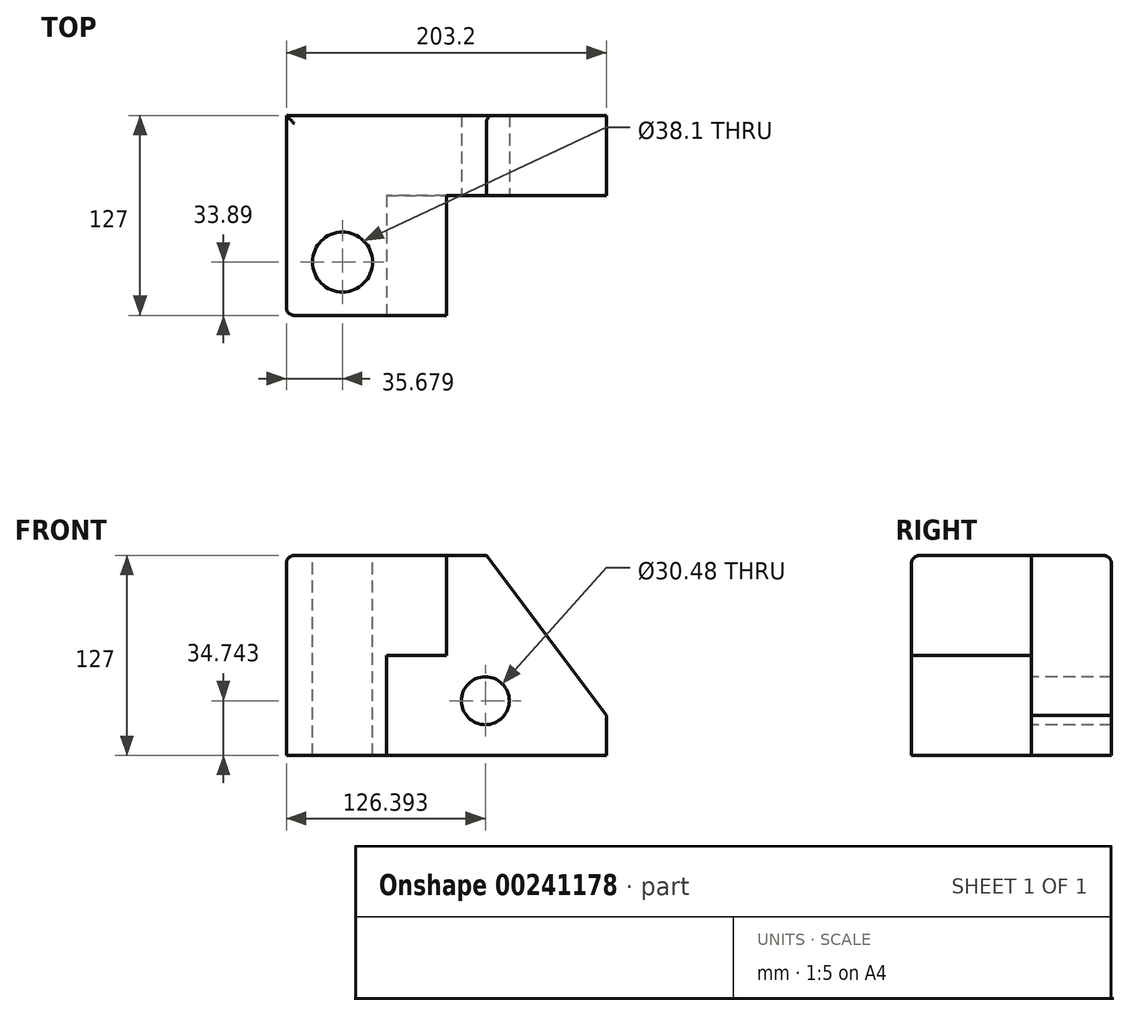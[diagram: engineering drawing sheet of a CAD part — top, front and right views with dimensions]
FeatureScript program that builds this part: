
annotation { "Feature Type Name" : "Feature", "Feature Type Description" : "" }
export const myFeature = defineFeature(function(context is Context, id is Id, definition is map)
    precondition{}
    {
        {
            var Q0;
            Q0=qCreatedBy(makeId("Front.planeOp"),FACE);
            var sketch = newSketch(context, id + "F0", { "sketchPlane" : qUnion([Q0])});
            skPoint(sketch, "E0.start.orphan", {"position": v(0, -60.78) * mm});
            skLineSegment(sketch, "E1", {"start": v(-88.74, -63.95) * mm, "end": v(114.46, -63.95) * mm});
            skLineSegment(sketch, "E2", {"start": v(114.46, -63.95) * mm, "end": v(114.46, 63.05) * mm});
            skLineSegment(sketch, "E3", {"start": v(-88.74, -63.95) * mm, "end": v(-88.74, 63.05) * mm});
            skLineSegment(sketch, "E4", {"start": v(-88.74, 63.05) * mm, "end": v(114.46, 63.05) * mm});
            skSolve(sketch);
        }
        {
            var Q0;
            Q0 = qSketchRegion(id + "F0", true);
            extrude(context, id + "F1", {"entities" : qUnion([Q0]), "depth" : 127 * mm});
        }
        {
            var Q0;
            Q0=makeQuery(id+"F1.opExtrude","CAP_FACE",FACE,{"disambiguationData":[OSD([sQuery(id+"F0.wireOp",EDGE,"E1"),sQuery(id+"F0.wireOp",EDGE,"E2"),sQuery(id+"F0.wireOp",EDGE,"E3"),sQuery(id+"F0.wireOp",EDGE,"E4")])],"isStart":false});
            var sketch = newSketch(context, id + "F2", { "sketchPlane" : qUnion([Q0])});
            skLineSegment(sketch, "E5", {"start": v(-88.74, 63.05) * mm, "end": v(12.86, 63.05) * mm});
            skLineSegment(sketch, "E6", {"start": v(12.86, 63.05) * mm, "end": v(12.86, -0.45) * mm});
            skLineSegment(sketch, "E7", {"start": v(12.86, -0.45) * mm, "end": v(-25.24, -0.45) * mm});
            skLineSegment(sketch, "E8", {"start": v(-25.24, -0.45) * mm, "end": v(-25.24, -63.95) * mm});
            skLineSegment(sketch, "E9", {"start": v(-25.24, -63.95) * mm, "end": v(-88.74, -63.95) * mm});
            skLineSegment(sketch, "E10", {"start": v(-88.74, -63.95) * mm, "end": v(-88.74, 63.05) * mm});
            skSolve(sketch);
        }
        {
            var Q0;
            {var subQ3=sQuery(id+"F2.wireOp",EDGE,"E6");Q0=makeQuery(id+"F2.imprint","IMPRINT",FACE,{"disambiguationData":[TD([[makeQuery(id+"F2.imprint","IMPRINT",EDGE,{"derivedFrom":subQ3}),1.0]])]});}
            extrude(context, id + "F3", {"entities" : qUnion([Q0]), "operationType" : NewBodyOperationType.REMOVE, "oppositeDirection" : true, "depth" : 76.2 * mm});
        }
        {
            var Q0;
            Q0=makeQuery(id+"F1.opExtrude","SWEPT_EDGE",EDGE,{"disambiguationData":[OSD([sQuery(id+"F0.wireOp",EDGE,"E2"),sQuery(id+"F0.wireOp",EDGE,"E4")])]});
            chamfer(context, id + "F4", {"entities" : qUnion([Q0]), "chamferType" : ChamferType.TWO_OFFSETS, "width1" : 76.2 * mm, "oppositeDirection" : false, "width2" : 101.6 * mm, "tangentPropagation" : true});
        }
        {
            var Q0;
            Q0=makeQuery(id+"F1.opExtrude","CAP_EDGE",EDGE,{"disambiguationData":[OSD([sQuery(id+"F0.wireOp",EDGE,"E4")])],"isStart":false});
            var Q1;
            Q1=makeQuery(id+"F1.opExtrude","SWEPT_EDGE",EDGE,{"disambiguationData":[OSD([sQuery(id+"F0.wireOp",EDGE,"E3"),sQuery(id+"F0.wireOp",EDGE,"E4")])]});
            var Q2;
            Q2=makeQuery(id+"F3.boolean.opBoolean","COPY",EDGE,{"derivedFrom":makeQuery(id+"F3.opExtrude","SWEPT_EDGE",EDGE,{"disambiguationData":[OSD([sQuery(id+"F0.wireOp",EDGE,"E4"),sQuery(id+"F2.wireOp",EDGE,"E5"),sQuery(id+"F2.wireOp",EDGE,"E6")])]})});
            var Q3;
            Q3=makeQuery(id+"F3.boolean.opBoolean","COPY",EDGE,{"derivedFrom":makeQuery(id+"F3.opExtrude","CAP_EDGE",EDGE,{"disambiguationData":[OSD([sQuery(id+"F0.wireOp",EDGE,"E4")])],"isStart":false})});
            var Q4;
            Q4=makeQuery(id+"F1.opExtrude","CAP_EDGE",EDGE,{"disambiguationData":[OSD([sQuery(id+"F0.wireOp",EDGE,"E4")])],"isStart":true});
            fillet(context, id + "F5", {"entities" : qUnion([Q0, Q1, Q2, Q3, Q4]), "radius" : 5.08 * mm, "tangentPropagation" : true, "allowEdgeOverflow" : false});
        }
        {
            var Q0;
            Q0=makeQuery(id+"F3.boolean.opBoolean","COPY",EDGE,{"derivedFrom":makeQuery(id+"F3.opExtrude","CAP_EDGE",EDGE,{"disambiguationData":[OSD([sQuery(id+"F2.wireOp",EDGE,"E8")])],"isStart":true})});
            var Q1;
            Q1=makeQuery(id+"F1.opExtrude","CAP_EDGE",EDGE,{"disambiguationData":[OSD([sQuery(id+"F0.wireOp",EDGE,"E3")])],"isStart":false});
            fillet(context, id + "F6", {"entities" : qUnion([Q0, Q1]), "radius" : 5.08 * mm, "tangentPropagation" : true, "allowEdgeOverflow" : false});
        }
        {
            var Q0;
            Q0=makeQuery(id+"F3.boolean.opBoolean","COPY",FACE,{"derivedFrom":makeQuery(id+"F3.opExtrude","CAP_FACE",FACE,{"disambiguationData":[OSD([sQuery(id+"F0.wireOp",EDGE,"E1"),sQuery(id+"F0.wireOp",EDGE,"E2"),sQuery(id+"F0.wireOp",EDGE,"E4"),sQuery(id+"F2.wireOp",EDGE,"E6"),sQuery(id+"F2.wireOp",EDGE,"E7"),sQuery(id+"F2.wireOp",EDGE,"E8")])],"isStart":false})});
            var sketch = newSketch(context, id + "F7", { "sketchPlane" : qUnion([Q0])});
            skCircle(sketch, "E11", {"center": v(37.65, -29.2) * mm, "radius": 15.24 * mm});
            skSolve(sketch);
        }
        {
            var Q0;
            Q0=makeQuery(id+"F7.imprint","IMPRINT",FACE,{"disambiguationData":[TD([[makeQuery(id+"F7.imprint","IMPRINT",EDGE,{"derivedFrom":sQuery(id+"F7.wireOp",EDGE,"E11")}),1.0]])]});
            var Q1;
            Q1=makeQuery(id+"F1.opExtrude","CAP_FACE",FACE,{"disambiguationData":[OSD([sQuery(id+"F0.wireOp",EDGE,"E1"),sQuery(id+"F0.wireOp",EDGE,"E2"),sQuery(id+"F0.wireOp",EDGE,"E3"),sQuery(id+"F0.wireOp",EDGE,"E4")])],"isStart":true});
            extrude(context, id + "F8", {"entities" : qUnion([Q0]), "operationType" : NewBodyOperationType.REMOVE, "endBound" : BoundingType.UP_TO_SURFACE, "oppositeDirection" : true, "endBoundEntityFace" : qUnion([Q1]), "depth" : 25.4 * mm});
        }
        {
            var Q0;
            Q0=makeQuery(id+"F1.opExtrude","SWEPT_FACE",FACE,{"disambiguationData":[OSD([sQuery(id+"F0.wireOp",EDGE,"E4")])]});
            var sketch = newSketch(context, id + "F9", { "sketchPlane" : qUnion([Q0])});
            skCircle(sketch, "E12", {"center": v(-53.06, -93.11) * mm, "radius": 19.05 * mm});
            skSolve(sketch);
        }
        {
            var Q0;
            Q0=makeQuery(id+"F9.imprint","IMPRINT",FACE,{"disambiguationData":[TD([[makeQuery(id+"F9.imprint","IMPRINT",EDGE,{"derivedFrom":sQuery(id+"F9.wireOp",EDGE,"E12")}),1.0]])]});
            var Q1;
            Q1=makeQuery(id+"F1.opExtrude","SWEPT_FACE",FACE,{"disambiguationData":[OSD([sQuery(id+"F0.wireOp",EDGE,"E1")])]});
            extrude(context, id + "F10", {"entities" : qUnion([Q0]), "operationType" : NewBodyOperationType.REMOVE, "endBound" : BoundingType.UP_TO_SURFACE, "oppositeDirection" : true, "endBoundEntityFace" : qUnion([Q1]), "depth" : 25.4 * mm});
        }
    });
